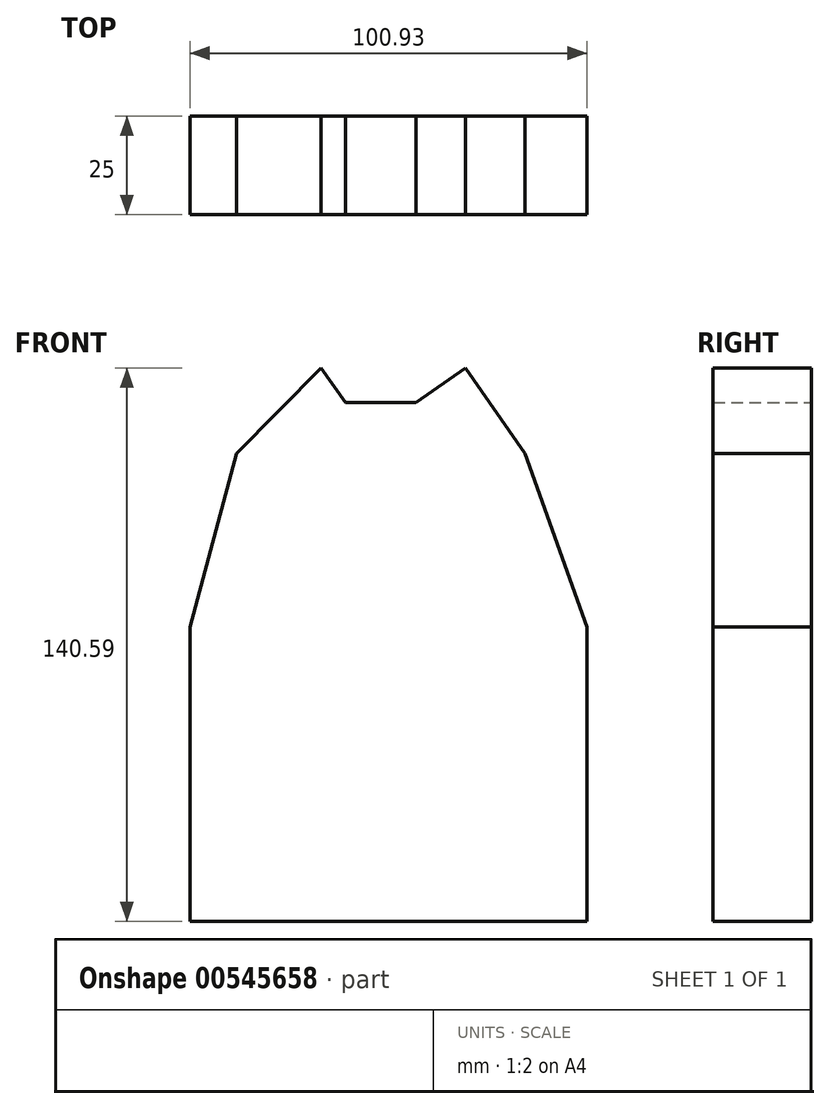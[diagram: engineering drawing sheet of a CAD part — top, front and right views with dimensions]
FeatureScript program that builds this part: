
annotation { "Feature Type Name" : "Feature", "Feature Type Description" : "" }
export const myFeature = defineFeature(function(context is Context, id is Id, definition is map)
    precondition{}
    {
        {
            var Q0;
            Q0=qCreatedBy(makeId("Front.planeOp"),FACE);
            var sketch = newSketch(context, id + "F0", { "sketchPlane" : qUnion([Q0])});
            skLineSegment(sketch, "E0", {"start": v(-48.93, -74.82) * mm, "end": v(52, -74.82) * mm});
            skLineSegment(sketch, "E1", {"start": v(52, -74.82) * mm, "end": v(0, 0) * mm});
            skLineSegment(sketch, "E2", {"start": v(0, 0) * mm, "end": v(-48.93, -74.82) * mm});
            skLineSegment(sketch, "E3", {"start": v(-48.93, 0) * mm, "end": v(0, 0) * mm});
            skLineSegment(sketch, "E4", {"start": v(52, 0) * mm, "end": v(52, -74.82) * mm});
            skLineSegment(sketch, "E5", {"start": v(-48.93, 0) * mm, "end": v(-48.93, -74.82) * mm});
            skLineSegment(sketch, "E6", {"start": v(0, 0) * mm, "end": v(52, 0) * mm});
            skLineSegment(sketch, "E7", {"start": v(52, 0) * mm, "end": v(36.2, 44.1) * mm});
            skLineSegment(sketch, "E8", {"start": v(36.2, 44.1) * mm, "end": v(21.14, 65.77) * mm});
            skLineSegment(sketch, "E9", {"start": v(21.14, 65.77) * mm, "end": v(0, 0) * mm});
            skLineSegment(sketch, "E10", {"start": v(36.2, 44.1) * mm, "end": v(0, 0) * mm});
            skLineSegment(sketch, "E11", {"start": v(21.14, 65.77) * mm, "end": v(8.46, 56.96) * mm});
            skLineSegment(sketch, "E12", {"start": v(8.46, 56.96) * mm, "end": v(-9.43, 56.96) * mm});
            skLineSegment(sketch, "E13", {"start": v(-9.43, 56.96) * mm, "end": v(-15.56, 65.77) * mm});
            skLineSegment(sketch, "E14", {"start": v(-15.56, 65.77) * mm, "end": v(-37.08, 44.1) * mm});
            skLineSegment(sketch, "E15", {"start": v(-37.08, 44.1) * mm, "end": v(-48.93, 0) * mm});
            skLineSegment(sketch, "E16", {"start": v(-37.08, 44.1) * mm, "end": v(0, 0) * mm});
            skLineSegment(sketch, "E17", {"start": v(-15.56, 65.77) * mm, "end": v(0, 0) * mm});
            skSolve(sketch);
        }
        {
            var Q0;
            Q0=makeQuery(id+"F0.imprint","IMPRINT",FACE,{"disambiguationData":[TD([[makeQuery(id+"F0.imprint","IMPRINT",EDGE,{"derivedFrom":sQuery(id+"F0.wireOp",EDGE,"E0")}),1.0]])]});
            var Q1;
            Q1=makeQuery(id+"F0.imprint","IMPRINT",FACE,{"disambiguationData":[TD([[makeQuery(id+"F0.imprint","IMPRINT",EDGE,{"derivedFrom":sQuery(id+"F0.wireOp",EDGE,"E2")}),-1.0]])]});
            var Q2;
            Q2=makeQuery(id+"F0.imprint","IMPRINT",FACE,{"disambiguationData":[TD([[makeQuery(id+"F0.imprint","IMPRINT",EDGE,{"derivedFrom":sQuery(id+"F0.wireOp",EDGE,"E14")}),1.0]])]});
            var Q3;
            Q3=makeQuery(id+"F0.imprint","IMPRINT",FACE,{"disambiguationData":[TD([[makeQuery(id+"F0.imprint","IMPRINT",EDGE,{"derivedFrom":sQuery(id+"F0.wireOp",EDGE,"E9")}),-1.0]])]});
            var Q4;
            Q4=makeQuery(id+"F0.imprint","IMPRINT",FACE,{"disambiguationData":[TD([[makeQuery(id+"F0.imprint","IMPRINT",EDGE,{"derivedFrom":sQuery(id+"F0.wireOp",EDGE,"E8")}),1.0]])]});
            var Q5;
            Q5=makeQuery(id+"F0.imprint","IMPRINT",FACE,{"disambiguationData":[TD([[makeQuery(id+"F0.imprint","IMPRINT",EDGE,{"derivedFrom":sQuery(id+"F0.wireOp",EDGE,"E6")}),1.0]])]});
            var Q6;
            Q6=makeQuery(id+"F0.imprint","IMPRINT",FACE,{"disambiguationData":[TD([[makeQuery(id+"F0.imprint","IMPRINT",EDGE,{"derivedFrom":sQuery(id+"F0.wireOp",EDGE,"E1")}),-1.0]])]});
            var Q7;
            Q7=makeQuery(id+"F0.imprint","IMPRINT",FACE,{"disambiguationData":[TD([[makeQuery(id+"F0.imprint","IMPRINT",EDGE,{"derivedFrom":sQuery(id+"F0.wireOp",EDGE,"E3")}),1.0]])]});
            extrude(context, id + "F1", {"entities" : qUnion([Q0, Q1, Q2, Q3, Q4, Q5, Q6, Q7]), "depth" : 25 * mm, "offsetDistance" : 25 * mm});
        }
    });
